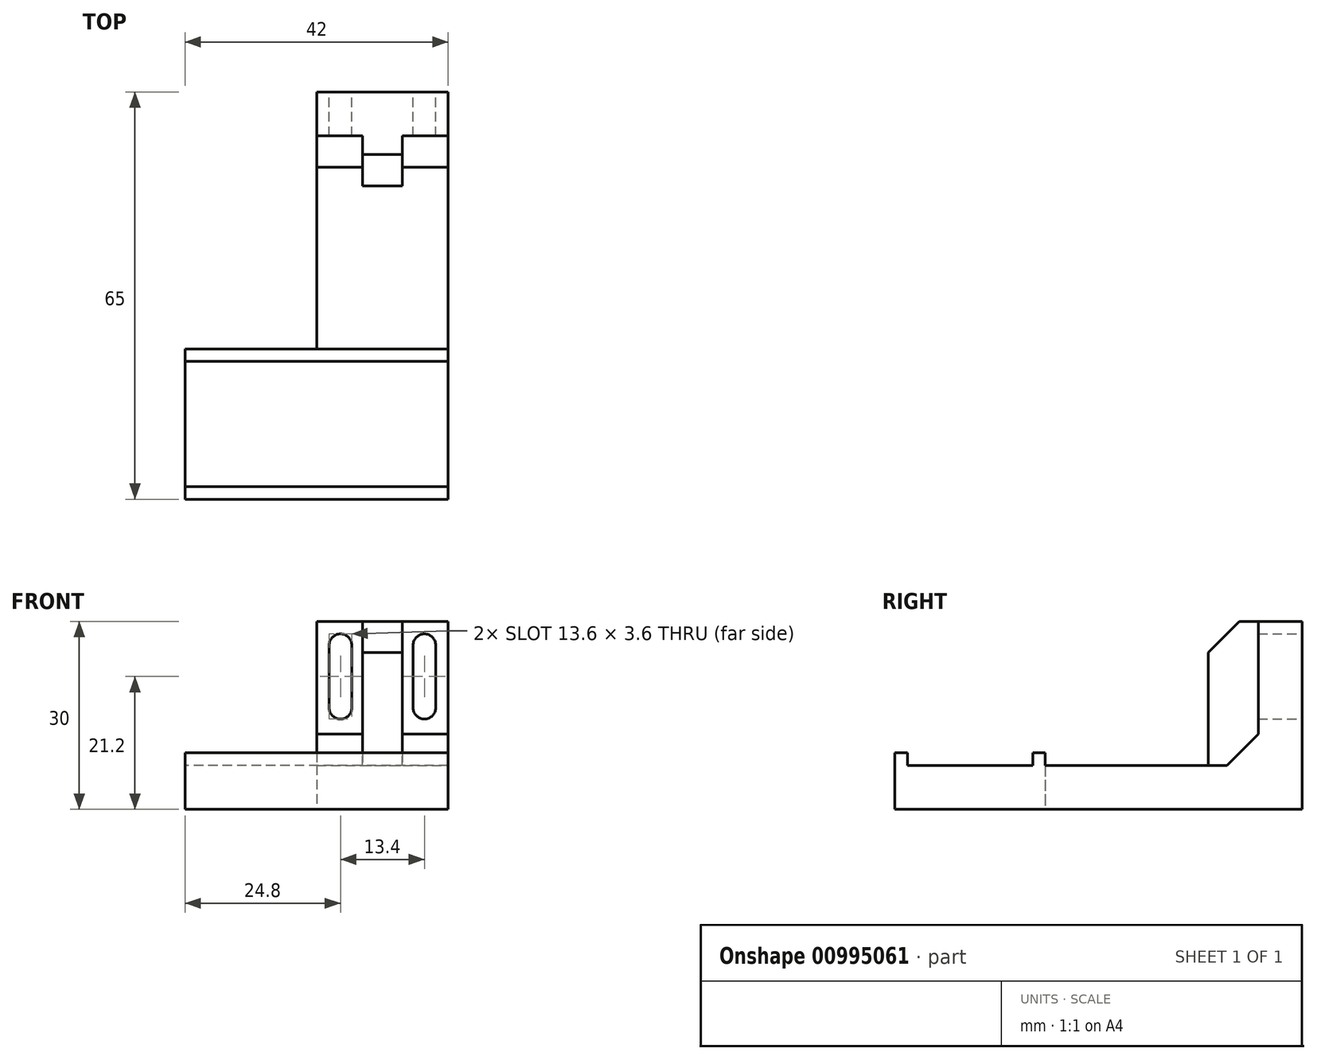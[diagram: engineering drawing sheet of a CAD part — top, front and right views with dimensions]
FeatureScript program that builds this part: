
annotation { "Feature Type Name" : "Feature", "Feature Type Description" : "" }
export const myFeature = defineFeature(function(context is Context, id is Id, definition is map)
    precondition{}
    {
        {
            var Q0;
            Q0=qCreatedBy(makeId("Right.planeOp"),FACE);
            var sketch = newSketch(context, id + "F0", { "sketchPlane" : qUnion([Q0])});
            skLineSegment(sketch, "E0", {"start": v(0, -23) * mm, "end": v(0, 0) * mm});
            skLineSegment(sketch, "E1", {"start": v(0, -23) * mm, "end": v(-46.5, -23) * mm});
            skLineSegment(sketch, "E2", {"start": v(-58, -23) * mm, "end": v(-58, -30) * mm});
            skLineSegment(sketch, "E3", {"start": v(0, 0) * mm, "end": v(7, 0) * mm});
            skLineSegment(sketch, "E4", {"start": v(-58, -23) * mm, "end": v(-51, -23) * mm});
            skLineSegment(sketch, "E5", {"start": v(-58, -30) * mm, "end": v(7, -30) * mm});
            skLineSegment(sketch, "E6", {"start": v(7, 0) * mm, "end": v(7, -30) * mm});
            skPoint(sketch, "E7.orphan", {"position": v(-58, -30) * mm});
            skLineSegment(sketch, "E8", {"start": v(-51, -23) * mm, "end": v(-46.5, -23) * mm});
            skSolve(sketch);
        }
        {
            var Q0;
            Q0=makeQuery(id+"F0.imprint","IMPRINT",FACE,{"disambiguationData":[TD([[makeQuery(id+"F0.imprint","IMPRINT",EDGE,{"derivedFrom":sQuery(id+"F0.wireOp",EDGE,"E0")}),-1.0]])]});
            extrude(context, id + "F1", {"entities" : qUnion([Q0]), "depth" : 10.5 * mm, "offsetDistance" : 25 * mm});
        }
        {
            var Q0;
            Q0=makeQuery(id+"FVBW8Jh66RSUQSt_1.boolean.opBoolean","MERGE",FACE,{"derivedFrom":[makeQuery(id+"F1.opExtrude","SWEPT_FACE",FACE,{"disambiguationData":[OSD([sQuery(id+"F0.wireOp",EDGE,"E6")])]}),makeQuery(id+"FVBW8Jh66RSUQSt_1.opExtrude","SWEPT_FACE",FACE,{"disambiguationData":[OSD([sQuery(id+"FXS95yzYIFY67fw_1.wireOp",EDGE,"b3a6df52-4f70-493d-badf-e32598c3f228.0.7")])]})]});
            var sketch = newSketch(context, id + "F2", { "sketchPlane" : qUnion([Q0])});
            skLineSegment(sketch, "E9.left", {"start": v(-4.9, -3.8) * mm, "end": v(-4.9, -13.8) * mm});
            skLineSegment(sketch, "E9.right", {"start": v(-8.5, -3.8) * mm, "end": v(-8.5, -13.8) * mm});
            skArc(sketch, "E10.filletArc", {"start": v(-8.5, -13.8) * mm, "mid": v(-6.7, -15.6) * mm, "end": v(-4.9, -13.8) * mm});
            skArc(sketch, "E11", {"start": v(-4.9, -3.8) * mm, "mid": v(-6.7, -2) * mm, "end": v(-8.5, -3.8) * mm});
            skLineSegment(sketch, "E12.bottom", {"start": v(0, 0) * mm, "end": v(-3.2, 0) * mm});
            skLineSegment(sketch, "E12.top", {"start": v(0, -23) * mm, "end": v(-3.2, -23) * mm});
            skLineSegment(sketch, "E12.left", {"start": v(0, 0) * mm, "end": v(0, -23) * mm});
            skLineSegment(sketch, "E12.right", {"start": v(-3.2, 0) * mm, "end": v(-3.2, -23) * mm});
            skSolve(sketch);
        }
        {
            var Q0;
            Q0=makeQuery(id+"F2.imprint","IMPRINT",FACE,{"disambiguationData":[TD([[makeQuery(id+"F2.imprint","IMPRINT",EDGE,{"derivedFrom":sQuery(id+"F2.wireOp",EDGE,"E9.left")}),-1.0]])]});
            extrude(context, id + "F3", {"entities" : qUnion([Q0]), "operationType" : NewBodyOperationType.REMOVE, "oppositeDirection" : true, "depth" : 25 * mm, "offsetDistance" : 25 * mm});
        }
        {
            var Q0;
            Q0=makeQuery(id+"F2.imprint","IMPRINT",FACE,{"disambiguationData":[TD([[makeQuery(id+"F2.imprint","IMPRINT",EDGE,{"derivedFrom":sQuery(id+"F2.wireOp",EDGE,"E12.bottom")}),-1.0]])]});
            extrude(context, id + "F4", {"entities" : qUnion([Q0]), "operationType" : NewBodyOperationType.ADD, "oppositeDirection" : true, "depth" : 15 * mm, "offsetDistance" : 25 * mm});
        }
        {
            var Q0;
            Q0=makeQuery(id+"FVBW8Jh66RSUQSt_1.boolean.opBoolean","MERGE",EDGE,{"derivedFrom":[makeQuery(id+"F1.opExtrude","SWEPT_EDGE",EDGE,{"disambiguationData":[OSD([sQuery(id+"F0.wireOp",EDGE,"E0"),sQuery(id+"F0.wireOp",EDGE,"E1")])]}),makeQuery(id+"FVBW8Jh66RSUQSt_1.opExtrude","SWEPT_EDGE",EDGE,{"disambiguationData":[OSD([sQuery(id+"FXS95yzYIFY67fw_1.wireOp",EDGE,"b3a6df52-4f70-493d-badf-e32598c3f228.0.9"),sQuery(id+"FXS95yzYIFY67fw_1.wireOp",EDGE,"scxdzQQM-Vcej-rqMY-N3gj-rb8Nq5E2PnR6")])]})]});
            var Q1;
            Q1=makeQuery(id+"F4.opExtrude","CAP_EDGE",EDGE,{"disambiguationData":[OSD([sQuery(id+"F2.wireOp",EDGE,"E12.top")])],"isStart":false});
            var Q2;
            Q2=makeQuery(id+"F4.opExtrude","CAP_EDGE",EDGE,{"disambiguationData":[OSD([sQuery(id+"F2.wireOp",EDGE,"E12.bottom")])],"isStart":false});
            chamfer(context, id + "F5", {"entities" : qUnion([Q0, Q1, Q2]), "width" : 5 * mm, "tangentPropagation" : true});
        }
        {
            var Q0;
            Q0=makeQuery(id+"F1.opExtrude","SWEPT_BODY",BODY,{"disambiguationData":[OSD([sQuery(id+"F0.wireOp",EDGE,"E0"),sQuery(id+"F0.wireOp",EDGE,"E1"),sQuery(id+"F0.wireOp",EDGE,"E2"),sQuery(id+"F0.wireOp",EDGE,"E3"),sQuery(id+"F0.wireOp",EDGE,"E4"),sQuery(id+"F0.wireOp",EDGE,"E5"),sQuery(id+"F0.wireOp",EDGE,"E6"),sQuery(id+"F0.wireOp",EDGE,"E8")])]});
            var Q1;
            Q1=makeQuery(id+"F4.boolean.opBoolean","MERGE",FACE,{"derivedFrom":[makeQuery(id+"F1.opExtrude","CAP_FACE",FACE,{"disambiguationData":[OSD([sQuery(id+"F0.wireOp",EDGE,"E0"),sQuery(id+"F0.wireOp",EDGE,"E1"),sQuery(id+"F0.wireOp",EDGE,"E2"),sQuery(id+"F0.wireOp",EDGE,"E3"),sQuery(id+"F0.wireOp",EDGE,"E4"),sQuery(id+"F0.wireOp",EDGE,"E5"),sQuery(id+"F0.wireOp",EDGE,"E6"),sQuery(id+"F0.wireOp",EDGE,"E8")])],"isStart":true}),makeQuery(id+"F4.opExtrude","SWEPT_FACE",FACE,{"disambiguationData":[OSD([sQuery(id+"F2.wireOp",EDGE,"E12.left")])]})]});
            mirror(context, id + "F6", {"operationType" : NewBodyOperationType.ADD, "entities" : qUnion([Q0]), "mirrorPlane" : qUnion([Q1])});
        }
        {
            var Q0;
            Q0=makeQuery(id+"F6.opPattern","COPY",FACE,{"derivedFrom":makeQuery(id+"F1.opExtrude","CAP_FACE",FACE,{"disambiguationData":[OSD([sQuery(id+"F0.wireOp",EDGE,"E0"),sQuery(id+"F0.wireOp",EDGE,"E1"),sQuery(id+"F0.wireOp",EDGE,"E2"),sQuery(id+"F0.wireOp",EDGE,"E3"),sQuery(id+"F0.wireOp",EDGE,"E4"),sQuery(id+"F0.wireOp",EDGE,"E5"),sQuery(id+"F0.wireOp",EDGE,"E6"),sQuery(id+"F0.wireOp",EDGE,"E8")])],"isStart":false}),"instanceName":"1"});
            var sketch = newSketch(context, id + "F7", { "sketchPlane" : qUnion([Q0])});
            skLineSegment(sketch, "E13", {"start": v(58, -30) * mm, "end": v(58, -21) * mm});
            skLineSegment(sketch, "E14", {"start": v(58, -21) * mm, "end": v(56, -21) * mm});
            skLineSegment(sketch, "E15", {"start": v(56, -21) * mm, "end": v(56, -23) * mm});
            skLineSegment(sketch, "E16", {"start": v(56, -23) * mm, "end": v(36, -23) * mm});
            skLineSegment(sketch, "E17", {"start": v(36, -23) * mm, "end": v(36, -21) * mm});
            skLineSegment(sketch, "E18", {"start": v(36, -21) * mm, "end": v(34, -21) * mm});
            skLineSegment(sketch, "E19", {"start": v(34, -21) * mm, "end": v(34, -30) * mm});
            skLineSegment(sketch, "E20", {"start": v(34, -30) * mm, "end": v(58, -30) * mm});
            skSolve(sketch);
        }
        {
            var Q0;
            Q0 = qSketchRegion(id + "F7", true);
            extrude(context, id + "F8", {"entities" : qUnion([Q0]), "operationType" : NewBodyOperationType.ADD, "endBound" : BoundingType.SYMMETRIC, "oppositeDirection" : true, "depth" : 42 * mm, "offsetDistance" : 25 * mm});
        }
    });
